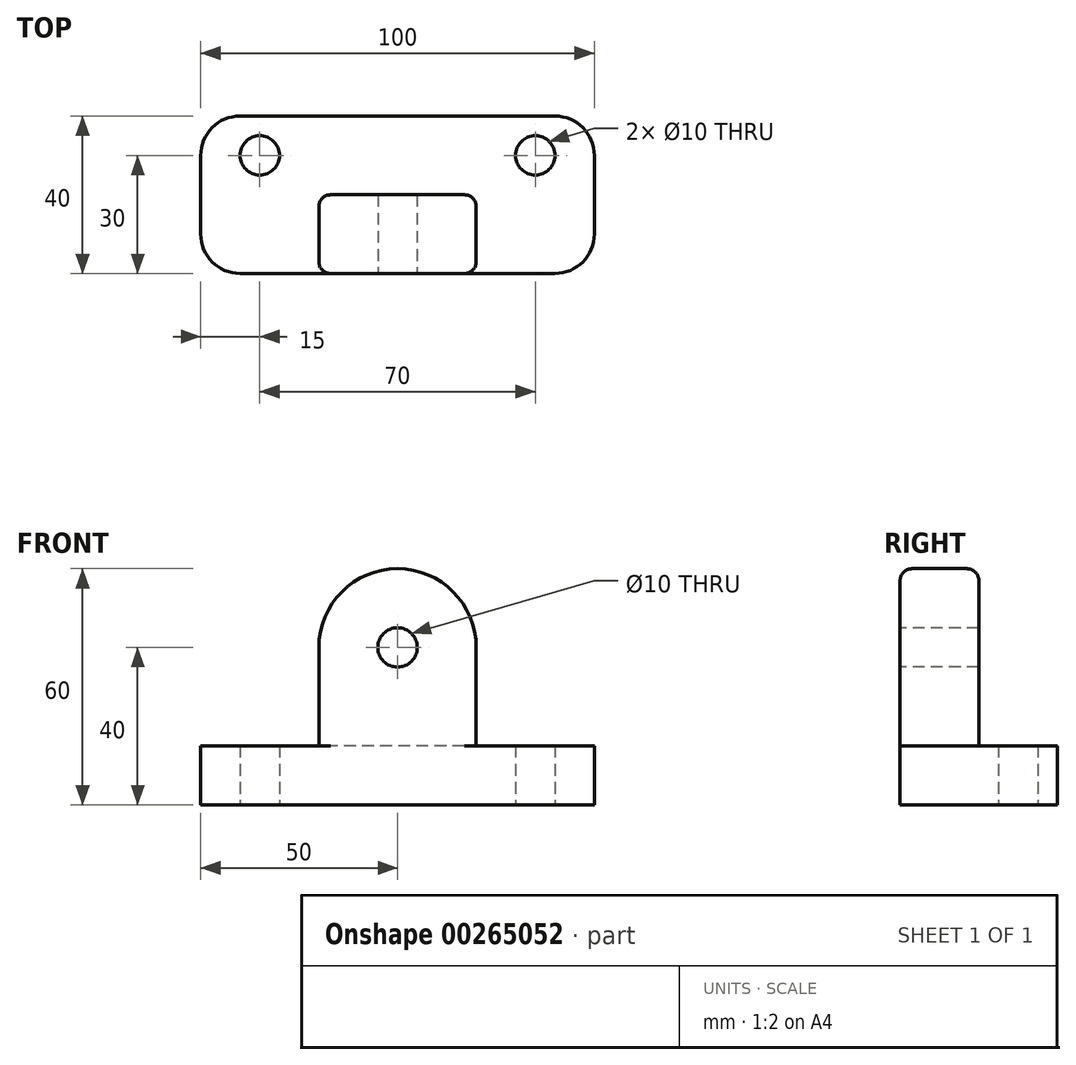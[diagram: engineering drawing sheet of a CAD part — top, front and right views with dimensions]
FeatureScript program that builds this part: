
annotation { "Feature Type Name" : "Feature", "Feature Type Description" : "" }
export const myFeature = defineFeature(function(context is Context, id is Id, definition is map)
    precondition{}
    {
        {
            var Q0;
            Q0=qCreatedBy(makeId("Top.planeOp"),FACE);
            var sketch = newSketch(context, id + "F0", { "sketchPlane" : qUnion([Q0])});
            skLineSegment(sketch, "E0.bottom", {"start": v(40, -20) * mm, "end": v(-40, -20) * mm});
            skLineSegment(sketch, "E0.top", {"start": v(40, 20) * mm, "end": v(-40, 20) * mm});
            skLineSegment(sketch, "E0.left", {"start": v(50, -10) * mm, "end": v(50, 10) * mm});
            skLineSegment(sketch, "E0.right", {"start": v(-50, -10) * mm, "end": v(-50, 10) * mm});
            skPoint(sketch, "E0.middle", {"position": v(0, 0) * mm});
            skPoint(sketch, "E1.visualSharp", {"position": v(-50, -20) * mm});
            skArc(sketch, "E1.filletArc", {"start": v(-50, -10) * mm, "mid": v(-47.07, -17.07) * mm, "end": v(-40, -20) * mm});
            skPoint(sketch, "E2.visualSharp", {"position": v(-50, 20) * mm});
            skArc(sketch, "E2.filletArc", {"start": v(-40, 20) * mm, "mid": v(-47.07, 17.07) * mm, "end": v(-50, 10) * mm});
            skPoint(sketch, "E3.visualSharp", {"position": v(50, 20) * mm});
            skArc(sketch, "E3.filletArc", {"start": v(50, 10) * mm, "mid": v(47.07, 17.07) * mm, "end": v(40, 20) * mm});
            skPoint(sketch, "E4.visualSharp", {"position": v(50, -20) * mm});
            skArc(sketch, "E4.filletArc", {"start": v(40, -20) * mm, "mid": v(47.07, -17.07) * mm, "end": v(50, -10) * mm});
            skLineSegment(sketch, "E5", {"start": v(-20.32, -20) * mm, "end": v(-20.32, 20) * mm});
            skLineSegment(sketch, "E6", {"start": v(19.68, -20) * mm, "end": v(19.68, 20) * mm});
            skCircle(sketch, "E7", {"center": v(-35, 10) * mm, "radius": 5 * mm});
            skCircle(sketch, "E8", {"center": v(35, 10) * mm, "radius": 5 * mm});
            skSolve(sketch);
        }
        {
            var Q0;
            Q0=makeQuery(id+"F0.imprint","IMPRINT",FACE,{"disambiguationData":[TD([[makeQuery(id+"F0.imprint","IMPRINT",EDGE,{"derivedFrom":sQuery(id+"F0.wireOp",EDGE,"E0.right")}),-1.0]])]});
            var Q1;
            {var subQ0=sQuery(id+"F0.wireOp",EDGE,"E5");Q1=makeQuery(id+"F0.imprint","IMPRINT",FACE,{"disambiguationData":[TD([[makeQuery(id+"F0.imprint","IMPRINT",EDGE,{"derivedFrom":subQ0}),-1.0]])]});}
            var Q2;
            Q2=makeQuery(id+"F0.imprint","IMPRINT",FACE,{"disambiguationData":[TD([[makeQuery(id+"F0.imprint","IMPRINT",EDGE,{"derivedFrom":sQuery(id+"F0.wireOp",EDGE,"E0.left")}),1.0]])]});
            extrude(context, id + "F1", {"entities" : qUnion([Q0, Q1, Q2]), "depth" : 15 * mm});
        }
        {
            var Q0;
            Q0=makeQuery(id+"F1.opExtrude","SWEPT_FACE",FACE,{"disambiguationData":[OSD([sQuery(id+"F0.wireOp",EDGE,"E0.bottom")])]});
            var sketch = newSketch(context, id + "F2", { "sketchPlane" : qUnion([Q0])});
            skLineSegment(sketch, "E9", {"start": v(-20, 40) * mm, "end": v(-20, 15) * mm});
            skLineSegment(sketch, "E10", {"start": v(20, 40) * mm, "end": v(20, 15) * mm});
            skCircle(sketch, "E11", {"center": v(0, 40) * mm, "radius": 5 * mm});
            skLineSegment(sketch, "E12", {"start": v(-20, 15) * mm, "end": v(20, 15) * mm});
            skArc(sketch, "E13", {"start": v(20, 40) * mm, "mid": v(0, 60) * mm, "end": v(-20, 40) * mm});
            skSolve(sketch);
        }
        {
            var Q0;
            Q0 = qSketchRegion(id + "F2", true);
            extrude(context, id + "F3", {"entities" : qUnion([Q0]), "operationType" : NewBodyOperationType.ADD, "oppositeDirection" : true, "depth" : 20 * mm});
        }
        {
            var Q0;
            Q0=makeQuery(id+"F3.opExtrude","CAP_EDGE",EDGE,{"disambiguationData":[OSD([sQuery(id+"F2.wireOp",EDGE,"E13")])],"isStart":false});
            var Q1;
            Q1=makeQuery(id+"F3.opExtrude","CAP_EDGE",EDGE,{"disambiguationData":[OSD([sQuery(id+"F2.wireOp",EDGE,"E12")])],"isStart":false});
            var Q2;
            Q2=makeQuery(id+"F3.opExtrude","CAP_EDGE",EDGE,{"disambiguationData":[OSD([sQuery(id+"F2.wireOp",EDGE,"E13")])],"isStart":true});
            fillet(context, id + "F4", {"entities" : qUnion([Q0, Q1, Q2]), "radius" : 3 * mm, "tangentPropagation" : true, "allowEdgeOverflow" : false});
        }
    });
